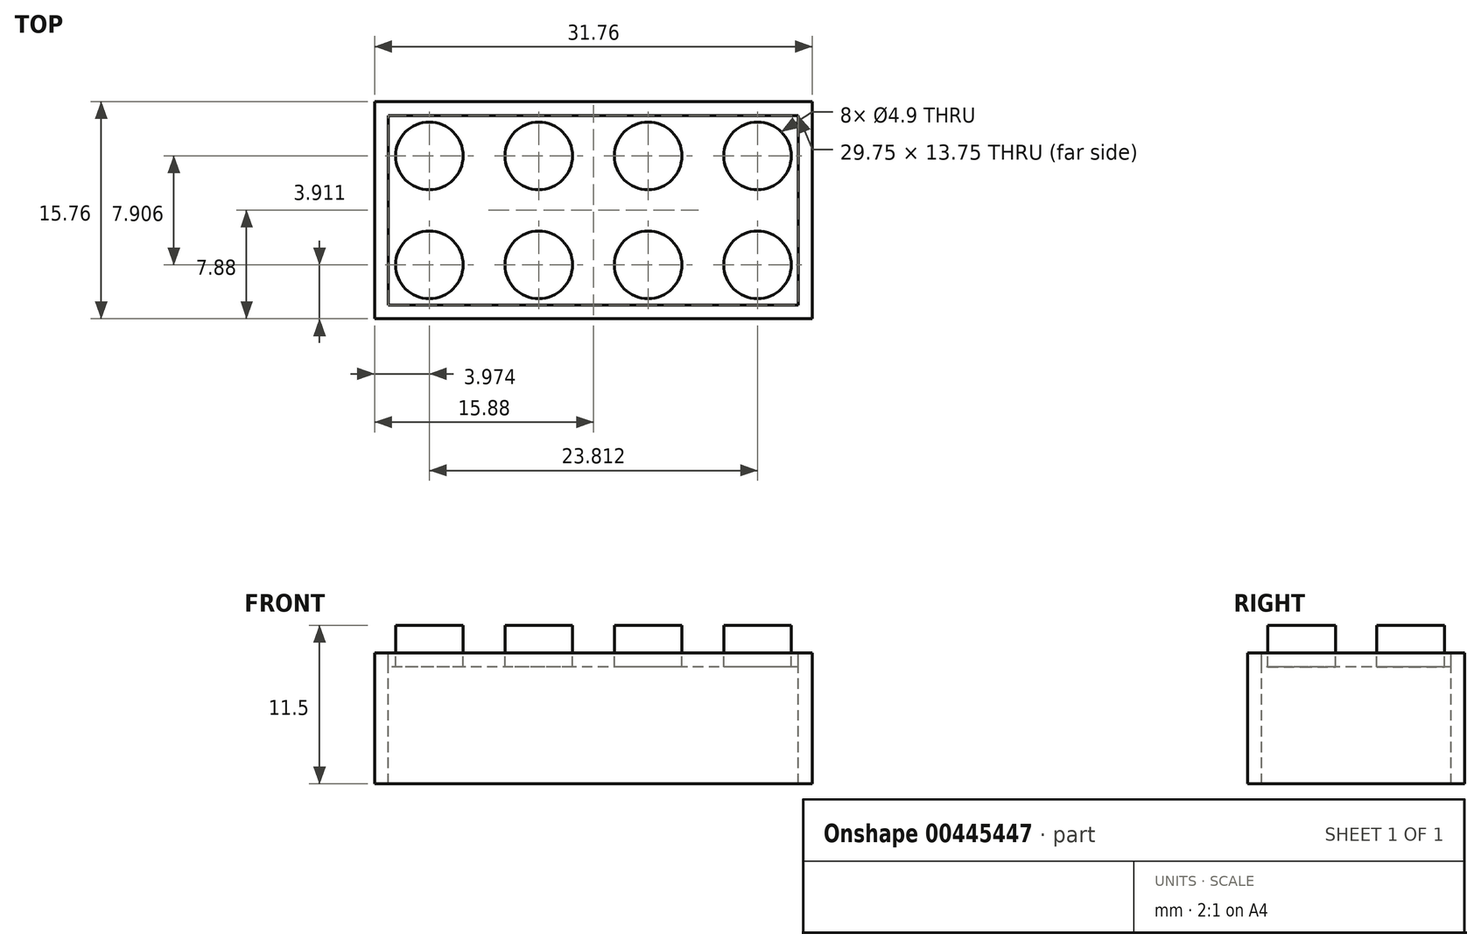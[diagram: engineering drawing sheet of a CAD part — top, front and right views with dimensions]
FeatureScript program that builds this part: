
annotation { "Feature Type Name" : "Feature", "Feature Type Description" : "" }
export const myFeature = defineFeature(function(context is Context, id is Id, definition is map)
    precondition{}
    {
        {
            var Q0;
            Q0=qCreatedBy(makeId("Top.planeOp"),FACE);
            var sketch = newSketch(context, id + "F0", { "sketchPlane" : qUnion([Q0])});
            skLineSegment(sketch, "E0.bottom", {"start": v(15.88, -7.87) * mm, "end": v(-15.88, -7.88) * mm});
            skLineSegment(sketch, "E0.top", {"start": v(15.88, 7.88) * mm, "end": v(-15.88, 7.88) * mm});
            skLineSegment(sketch, "E0.left", {"start": v(15.88, -7.87) * mm, "end": v(15.88, 7.88) * mm});
            skLineSegment(sketch, "E0.right", {"start": v(-15.88, -7.88) * mm, "end": v(-15.88, 7.88) * mm});
            skPoint(sketch, "E0.middle", {"position": v(0, 0) * mm});
            skLineSegment(sketch, "E1", {"start": v(0, 0) * mm, "end": v(0, 3.94) * mm});
            skLineSegment(sketch, "E2", {"start": v(0, 0) * mm, "end": v(0, -3.97) * mm});
            skLineSegment(sketch, "E3", {"start": v(0, 3.94) * mm, "end": v(3.97, 3.94) * mm});
            skLineSegment(sketch, "E4", {"start": v(0, 3.94) * mm, "end": v(-3.97, 3.94) * mm});
            skCircle(sketch, "E5", {"center": v(-3.97, 3.94) * mm, "radius": 2.45 * mm});
            skCircle(sketch, "E6", {"center": v(3.97, 3.94) * mm, "radius": 2.45 * mm});
            skLineSegment(sketch, "E7", {"start": v(-3.97, 3.94) * mm, "end": v(-11.9, 3.94) * mm});
            skLineSegment(sketch, "E8", {"start": v(3.97, 3.94) * mm, "end": v(11.9, 3.94) * mm});
            skCircle(sketch, "E9", {"center": v(-11.9, 3.94) * mm, "radius": 2.45 * mm});
            skCircle(sketch, "E10", {"center": v(11.9, 3.94) * mm, "radius": 2.45 * mm});
            skLineSegment(sketch, "E11", {"start": v(0, -3.97) * mm, "end": v(3.97, -3.97) * mm});
            skLineSegment(sketch, "E12", {"start": v(0, -3.97) * mm, "end": v(-3.97, -3.97) * mm});
            skCircle(sketch, "E13", {"center": v(-3.97, -3.97) * mm, "radius": 2.45 * mm});
            skCircle(sketch, "E14", {"center": v(3.97, -3.97) * mm, "radius": 2.45 * mm});
            skLineSegment(sketch, "E15", {"start": v(-3.97, -3.97) * mm, "end": v(-11.9, -3.97) * mm});
            skLineSegment(sketch, "E16", {"start": v(3.97, -3.97) * mm, "end": v(11.9, -3.97) * mm});
            skCircle(sketch, "E17", {"center": v(-11.9, -3.97) * mm, "radius": 2.45 * mm});
            skCircle(sketch, "E18", {"center": v(11.9, -3.97) * mm, "radius": 2.45 * mm});
            skLineSegment(sketch, "E19.bottom", {"start": v(14.88, 6.87) * mm, "end": v(-14.88, 6.88) * mm});
            skLineSegment(sketch, "E19.top", {"start": v(14.88, -6.88) * mm, "end": v(-14.88, -6.87) * mm});
            skLineSegment(sketch, "E19.left", {"start": v(14.88, 6.87) * mm, "end": v(14.88, -6.88) * mm});
            skLineSegment(sketch, "E19.right", {"start": v(-14.87, 6.88) * mm, "end": v(-14.88, -6.87) * mm});
            skSolve(sketch);
        }
        {
            var Q0;
            Q0=makeQuery(id+"F0.imprint","IMPRINT",FACE,{"disambiguationData":[TD([[makeQuery(id+"F0.imprint","IMPRINT",EDGE,{"derivedFrom":sQuery(id+"F0.wireOp",EDGE,"E9")}),1.0]])]});
            var Q1;
            {var subQ0=sQuery(id+"F0.wireOp",EDGE,"E7");var subQ1=sQuery(id+"F0.wireOp",EDGE,"E4");var subQ2=makeQuery(id+"F0.imprint","INTERSECT",VERTEX,{"derivedFrom":[subQ1,subQ0]});Q1=makeQuery(id+"F0.imprint","IMPRINT",FACE,{"disambiguationData":[TD([[makeQuery(id+"F0.imprint","IMPRINT",EDGE,{"disambiguationData":[TD([[subQ2,1.0]])],"derivedFrom":subQ1}),-1.0]])]});}
            var Q2;
            {var subQ0=sQuery(id+"F0.wireOp",EDGE,"E7");var subQ1=sQuery(id+"F0.wireOp",EDGE,"E4");var subQ2=makeQuery(id+"F0.imprint","INTERSECT",VERTEX,{"derivedFrom":[subQ1,subQ0]});Q2=makeQuery(id+"F0.imprint","IMPRINT",FACE,{"disambiguationData":[TD([[makeQuery(id+"F0.imprint","IMPRINT",EDGE,{"disambiguationData":[TD([[subQ2,1.0]])],"derivedFrom":subQ1}),1.0]])]});}
            var Q3;
            {var subQ0=sQuery(id+"F0.wireOp",EDGE,"E8");var subQ1=sQuery(id+"F0.wireOp",EDGE,"E3");var subQ2=makeQuery(id+"F0.imprint","INTERSECT",VERTEX,{"derivedFrom":[subQ1,subQ0]});Q3=makeQuery(id+"F0.imprint","IMPRINT",FACE,{"disambiguationData":[TD([[makeQuery(id+"F0.imprint","IMPRINT",EDGE,{"disambiguationData":[TD([[subQ2,1.0]])],"derivedFrom":subQ1}),-1.0]])]});}
            var Q4;
            Q4=makeQuery(id+"F0.imprint","IMPRINT",FACE,{"disambiguationData":[TD([[makeQuery(id+"F0.imprint","IMPRINT",EDGE,{"derivedFrom":sQuery(id+"F0.wireOp",EDGE,"E10")}),1.0]])]});
            var Q5;
            {var subQ0=sQuery(id+"F0.wireOp",EDGE,"E8");var subQ1=sQuery(id+"F0.wireOp",EDGE,"E3");var subQ2=makeQuery(id+"F0.imprint","INTERSECT",VERTEX,{"derivedFrom":[subQ1,subQ0]});Q5=makeQuery(id+"F0.imprint","IMPRINT",FACE,{"disambiguationData":[TD([[makeQuery(id+"F0.imprint","IMPRINT",EDGE,{"disambiguationData":[TD([[subQ2,1.0]])],"derivedFrom":subQ1}),1.0]])]});}
            var Q6;
            Q6=makeQuery(id+"F0.imprint","IMPRINT",FACE,{"disambiguationData":[TD([[makeQuery(id+"F0.imprint","IMPRINT",EDGE,{"derivedFrom":sQuery(id+"F0.wireOp",EDGE,"E17")}),1.0]])]});
            var Q7;
            {var subQ0=sQuery(id+"F0.wireOp",EDGE,"E15");var subQ1=sQuery(id+"F0.wireOp",EDGE,"E12");var subQ2=makeQuery(id+"F0.imprint","INTERSECT",VERTEX,{"derivedFrom":[subQ1,subQ0]});Q7=makeQuery(id+"F0.imprint","IMPRINT",FACE,{"disambiguationData":[TD([[makeQuery(id+"F0.imprint","IMPRINT",EDGE,{"disambiguationData":[TD([[subQ2,1.0]])],"derivedFrom":subQ1}),-1.0]])]});}
            var Q8;
            {var subQ0=sQuery(id+"F0.wireOp",EDGE,"E15");var subQ1=sQuery(id+"F0.wireOp",EDGE,"E12");var subQ2=makeQuery(id+"F0.imprint","INTERSECT",VERTEX,{"derivedFrom":[subQ1,subQ0]});Q8=makeQuery(id+"F0.imprint","IMPRINT",FACE,{"disambiguationData":[TD([[makeQuery(id+"F0.imprint","IMPRINT",EDGE,{"disambiguationData":[TD([[subQ2,1.0]])],"derivedFrom":subQ1}),1.0]])]});}
            var Q9;
            {var subQ0=sQuery(id+"F0.wireOp",EDGE,"E16");var subQ1=sQuery(id+"F0.wireOp",EDGE,"E11");var subQ2=makeQuery(id+"F0.imprint","INTERSECT",VERTEX,{"derivedFrom":[subQ1,subQ0]});Q9=makeQuery(id+"F0.imprint","IMPRINT",FACE,{"disambiguationData":[TD([[makeQuery(id+"F0.imprint","IMPRINT",EDGE,{"disambiguationData":[TD([[subQ2,1.0]])],"derivedFrom":subQ1}),-1.0]])]});}
            var Q10;
            {var subQ0=sQuery(id+"F0.wireOp",EDGE,"E16");var subQ1=sQuery(id+"F0.wireOp",EDGE,"E11");var subQ2=makeQuery(id+"F0.imprint","INTERSECT",VERTEX,{"derivedFrom":[subQ1,subQ0]});Q10=makeQuery(id+"F0.imprint","IMPRINT",FACE,{"disambiguationData":[TD([[makeQuery(id+"F0.imprint","IMPRINT",EDGE,{"disambiguationData":[TD([[subQ2,1.0]])],"derivedFrom":subQ1}),1.0]])]});}
            var Q11;
            Q11=makeQuery(id+"F0.imprint","IMPRINT",FACE,{"disambiguationData":[TD([[makeQuery(id+"F0.imprint","IMPRINT",EDGE,{"derivedFrom":sQuery(id+"F0.wireOp",EDGE,"E18")}),1.0]])]});
            extrude(context, id + "F1", {"entities" : qUnion([Q0, Q1, Q2, Q3, Q4, Q5, Q6, Q7, Q8, Q9, Q10, Q11]), "depth" : 2 * mm});
        }
        {
            var Q0;
            Q0=makeQuery(id+"F0.imprint","IMPRINT",FACE,{"disambiguationData":[TD([[makeQuery(id+"F0.imprint","IMPRINT",EDGE,{"derivedFrom":sQuery(id+"F0.wireOp",EDGE,"E9")}),-1.0]])]});
            extrude(context, id + "F2", {"entities" : qUnion([Q0]), "oppositeDirection" : true, "depth" : 1 * mm});
        }
        {
            var Q0;
            Q0=makeQuery(id+"F0.imprint","IMPRINT",FACE,{"disambiguationData":[TD([[makeQuery(id+"F0.imprint","IMPRINT",EDGE,{"derivedFrom":sQuery(id+"F0.wireOp",EDGE,"E0.bottom")}),-1.0]])]});
            extrude(context, id + "F3", {"entities" : qUnion([Q0]), "oppositeDirection" : true, "depth" : 9.5 * mm});
        }
    });
